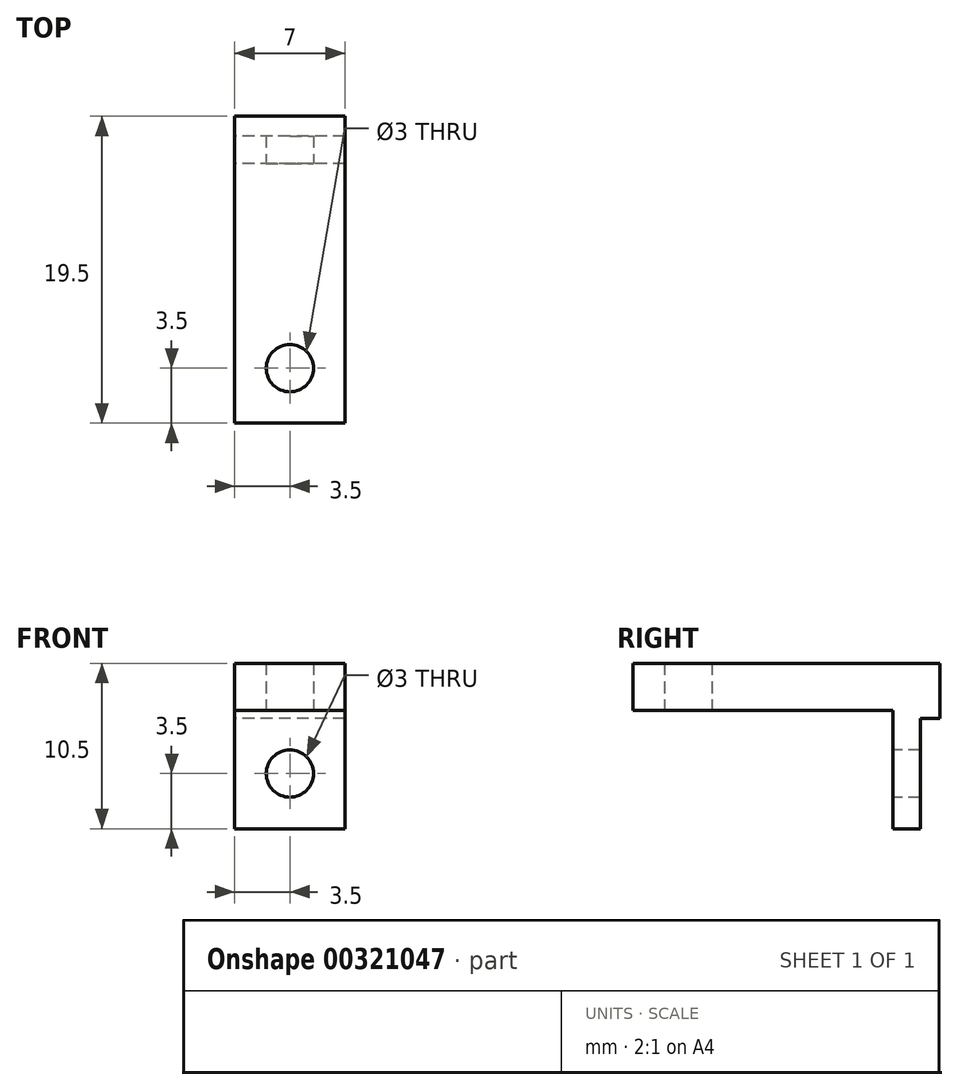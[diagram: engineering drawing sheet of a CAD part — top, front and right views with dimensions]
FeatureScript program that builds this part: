
annotation { "Feature Type Name" : "Feature", "Feature Type Description" : "" }
export const myFeature = defineFeature(function(context is Context, id is Id, definition is map)
    precondition{}
    {
        {
            var Q0;
            Q0=qCreatedBy(makeId("Front.planeOp"),FACE);
            var sketch = newSketch(context, id + "F0", { "sketchPlane" : qUnion([Q0])});
            skLineSegment(sketch, "E0.bottom", {"start": v(3.5, 5.25) * mm, "end": v(-3.5, 5.25) * mm});
            skLineSegment(sketch, "E0.top", {"start": v(3.5, -5.25) * mm, "end": v(-3.5, -5.25) * mm});
            skLineSegment(sketch, "E0.left", {"start": v(3.5, 5.25) * mm, "end": v(3.5, -5.25) * mm});
            skLineSegment(sketch, "E0.right", {"start": v(-3.5, 5.25) * mm, "end": v(-3.5, -5.25) * mm});
            skPoint(sketch, "E0.middle", {"position": v(0, 0) * mm});
            skSolve(sketch);
        }
        {
            var Q0;
            Q0 = qSketchRegion(id + "F0", true);
            extrude(context, id + "F1", {"entities" : qUnion([Q0]), "depth" : 3 * mm});
        }
        {
            var Q0;
            Q0=makeQuery(id+"F1.opExtrude","CAP_FACE",FACE,{"disambiguationData":[OSD([sQuery(id+"F0.wireOp",EDGE,"E0.bottom"),sQuery(id+"F0.wireOp",EDGE,"E0.top"),sQuery(id+"F0.wireOp",EDGE,"E0.left"),sQuery(id+"F0.wireOp",EDGE,"E0.right")])],"isStart":false});
            var sketch = newSketch(context, id + "F2", { "sketchPlane" : qUnion([Q0])});
            skLineSegment(sketch, "E1.bottom", {"start": v(-3.5, 5.25) * mm, "end": v(3.5, 5.25) * mm});
            skLineSegment(sketch, "E1.top", {"start": v(-3.5, 2.25) * mm, "end": v(3.5, 2.25) * mm});
            skLineSegment(sketch, "E1.left", {"start": v(-3.5, 5.25) * mm, "end": v(-3.5, 2.25) * mm});
            skLineSegment(sketch, "E1.right", {"start": v(3.5, 5.25) * mm, "end": v(3.5, 2.25) * mm});
            skSolve(sketch);
        }
        {
            var Q0;
            Q0 = qSketchRegion(id + "F2", true);
            extrude(context, id + "F3", {"entities" : qUnion([Q0]), "operationType" : NewBodyOperationType.ADD, "depth" : (17.75 - 1.25) * mm});
        }
        {
            var Q0;
            Q0=makeQuery(id+"F1.opExtrude","CAP_FACE",FACE,{"disambiguationData":[OSD([sQuery(id+"F0.wireOp",EDGE,"E0.bottom"),sQuery(id+"F0.wireOp",EDGE,"E0.top"),sQuery(id+"F0.wireOp",EDGE,"E0.left"),sQuery(id+"F0.wireOp",EDGE,"E0.right")])],"isStart":false});
            var sketch = newSketch(context, id + "F4", { "sketchPlane" : qUnion([Q0])});
            skCircle(sketch, "E2", {"center": v(0, -1.75) * mm, "radius": 1.5 * mm});
            skSolve(sketch);
        }
        {
            var Q0;
            Q0 = qSketchRegion(id + "F4", true);
            extrude(context, id + "F5", {"entities" : qUnion([Q0]), "operationType" : NewBodyOperationType.REMOVE, "oppositeDirection" : true, "depth" : 25 * mm});
        }
        {
            var Q0;
            Q0=makeQuery(id+"F3.opExtrude","SWEPT_FACE",FACE,{"disambiguationData":[OSD([sQuery(id+"F2.wireOp",EDGE,"E1.top")])]});
            var sketch = newSketch(context, id + "F6", { "sketchPlane" : qUnion([Q0])});
            skCircle(sketch, "E3", {"center": v(0, 16) * mm, "radius": 1.5 * mm});
            skSolve(sketch);
        }
        {
            var Q0;
            Q0 = qSketchRegion(id + "F6", true);
            extrude(context, id + "F7", {"entities" : qUnion([Q0]), "operationType" : NewBodyOperationType.REMOVE, "oppositeDirection" : true, "depth" : 25 * mm});
        }
        {
            var Q0;
            Q0=makeQuery(id+"F1.opExtrude","CAP_FACE",FACE,{"disambiguationData":[OSD([sQuery(id+"F0.wireOp",EDGE,"E0.bottom"),sQuery(id+"F0.wireOp",EDGE,"E0.top"),sQuery(id+"F0.wireOp",EDGE,"E0.left"),sQuery(id+"F0.wireOp",EDGE,"E0.right")])],"isStart":true});
            var sketch = newSketch(context, id + "F8", { "sketchPlane" : qUnion([Q0])});
            skLineSegment(sketch, "E4.bottom", {"start": v(-3.5, -5.25) * mm, "end": v(3.5, -5.25) * mm});
            skLineSegment(sketch, "E4.top", {"start": v(-3.5, 1.75) * mm, "end": v(3.5, 1.75) * mm});
            skLineSegment(sketch, "E4.left", {"start": v(-3.5, -5.25) * mm, "end": v(-3.5, 1.75) * mm});
            skLineSegment(sketch, "E4.right", {"start": v(3.5, -5.25) * mm, "end": v(3.5, 1.75) * mm});
            skSolve(sketch);
        }
        {
            var Q0;
            Q0 = qSketchRegion(id + "F8", true);
            extrude(context, id + "F9", {"entities" : qUnion([Q0]), "operationType" : NewBodyOperationType.REMOVE, "oppositeDirection" : true, "depth" : 1.25 * mm});
        }
    });
